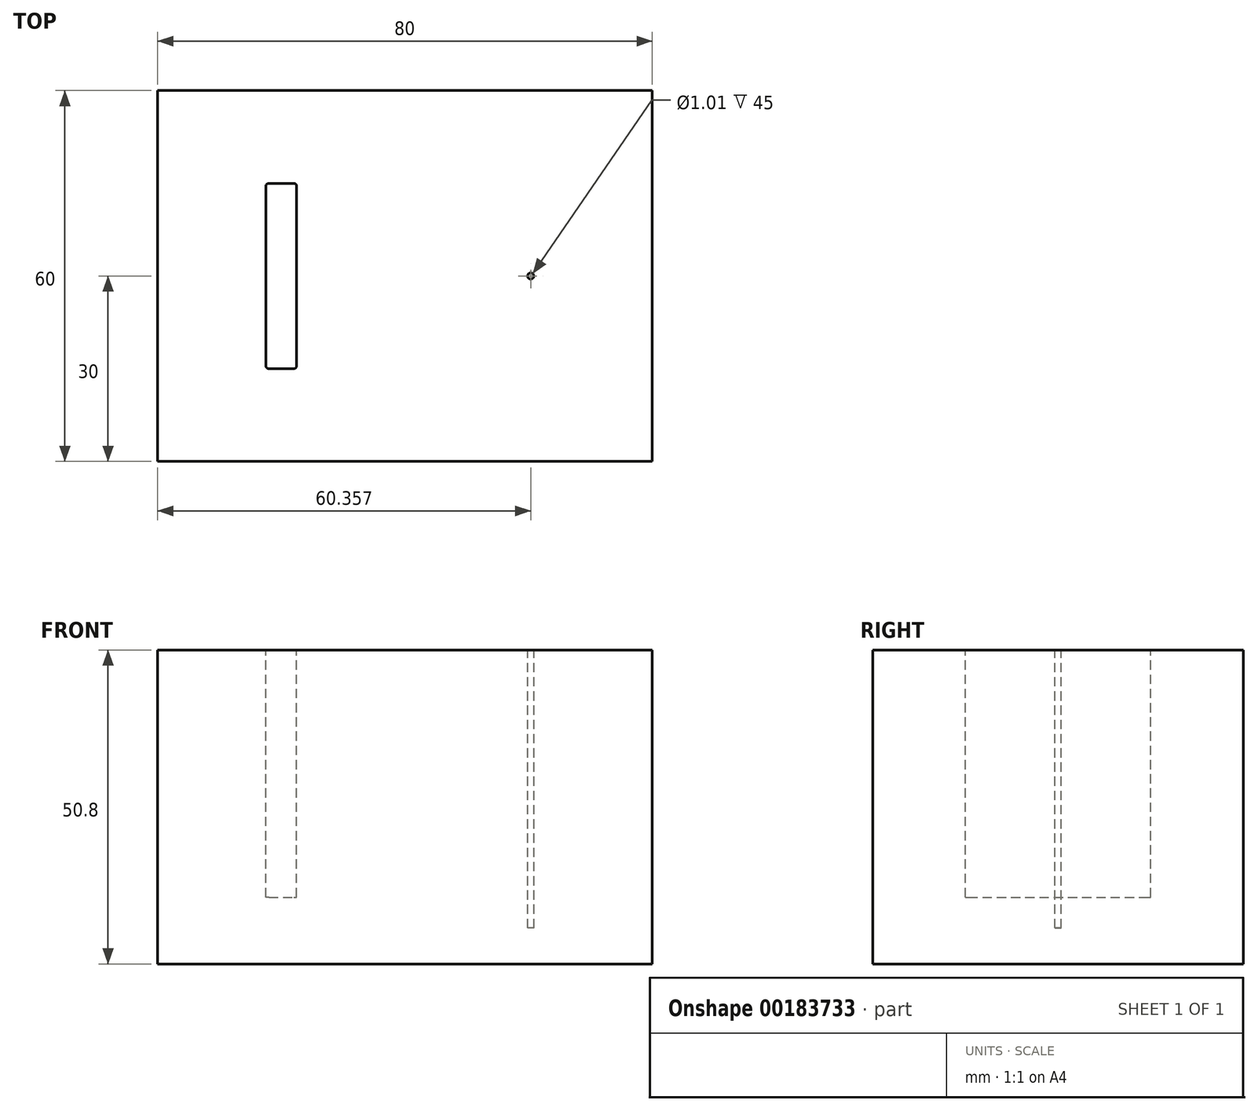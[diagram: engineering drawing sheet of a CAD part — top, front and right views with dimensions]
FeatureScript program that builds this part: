
annotation { "Feature Type Name" : "Feature", "Feature Type Description" : "" }
export const myFeature = defineFeature(function(context is Context, id is Id, definition is map)
    precondition{}
    {
        {
            var Q0;
            Q0=qCreatedBy(makeId("Top.planeOp"),FACE);
            var sketch = newSketch(context, id + "F0", { "sketchPlane" : qUnion([Q0])});
            skLineSegment(sketch, "E0.bottom", {"start": v(-40, -30) * mm, "end": v(40, -30) * mm});
            skLineSegment(sketch, "E0.top", {"start": v(-40, 30) * mm, "end": v(40, 30) * mm});
            skLineSegment(sketch, "E0.left", {"start": v(-40, -30) * mm, "end": v(-40, 30) * mm});
            skLineSegment(sketch, "E0.right", {"start": v(40, -30) * mm, "end": v(40, 30) * mm});
            skPoint(sketch, "E0.middle", {"position": v(0, 0) * mm});
            skSolve(sketch);
        }
        {
            var Q0;
            Q0=makeQuery(id+"F0.imprint","IMPRINT",FACE,{"disambiguationData":[TD([[makeQuery(id+"F0.imprint","IMPRINT",EDGE,{"derivedFrom":sQuery(id+"F0.wireOp",EDGE,"E0.bottom")}),1.0]])]});
            extrude(context, id + "F1", {"entities" : qUnion([Q0]), "depth" : 50.8 * mm});
        }
        {
            var Q0;
            Q0=makeQuery(id+"F1.opExtrude","CAP_FACE",FACE,{"disambiguationData":[OSD([sQuery(id+"F0.wireOp",EDGE,"E0.bottom"),sQuery(id+"F0.wireOp",EDGE,"E0.top"),sQuery(id+"F0.wireOp",EDGE,"E0.left"),sQuery(id+"F0.wireOp",EDGE,"E0.right")])],"isStart":false});
            var sketch = newSketch(context, id + "F2", { "sketchPlane" : qUnion([Q0])});
            skLineSegment(sketch, "E1.bottom", {"start": v(-22.5, -15) * mm, "end": v(-17.5, -15) * mm});
            skLineSegment(sketch, "E1.top", {"start": v(-22.5, 15) * mm, "end": v(-17.5, 15) * mm});
            skLineSegment(sketch, "E1.left", {"start": v(-22.5, -15) * mm, "end": v(-22.5, 15) * mm});
            skLineSegment(sketch, "E1.right", {"start": v(-17.5, -15) * mm, "end": v(-17.5, 15) * mm});
            skPoint(sketch, "E1.middle", {"position": v(-20, 0) * mm});
            skSolve(sketch);
        }
        {
            var Q0;
            Q0=makeQuery(id+"F2.imprint","IMPRINT",FACE,{"disambiguationData":[TD([[makeQuery(id+"F2.imprint","IMPRINT",EDGE,{"derivedFrom":sQuery(id+"F2.wireOp",EDGE,"E1.bottom")}),1.0]])]});
            extrude(context, id + "F3", {"entities" : qUnion([Q0]), "operationType" : NewBodyOperationType.REMOVE, "oppositeDirection" : true, "depth" : 40 * mm});
        }
        {
            var Q0;
            Q0=makeQuery(id+"F3.boolean.opBoolean","COPY",EDGE,{"derivedFrom":makeQuery(id+"F3.opExtrude","SWEPT_EDGE",EDGE,{"disambiguationData":[OSD([sQuery(id+"F2.wireOp",EDGE,"E1.top"),sQuery(id+"F2.wireOp",EDGE,"E1.left")])]})});
            var Q1;
            Q1=makeQuery(id+"F3.boolean.opBoolean","COPY",EDGE,{"derivedFrom":makeQuery(id+"F3.opExtrude","SWEPT_EDGE",EDGE,{"disambiguationData":[OSD([sQuery(id+"F2.wireOp",EDGE,"E1.top"),sQuery(id+"F2.wireOp",EDGE,"E1.right")])]})});
            var Q2;
            Q2=makeQuery(id+"F3.boolean.opBoolean","COPY",EDGE,{"derivedFrom":makeQuery(id+"F3.opExtrude","SWEPT_EDGE",EDGE,{"disambiguationData":[OSD([sQuery(id+"F2.wireOp",EDGE,"E1.bottom"),sQuery(id+"F2.wireOp",EDGE,"E1.left")])]})});
            var Q3;
            Q3=makeQuery(id+"F3.boolean.opBoolean","COPY",EDGE,{"derivedFrom":makeQuery(id+"F3.opExtrude","SWEPT_EDGE",EDGE,{"disambiguationData":[OSD([sQuery(id+"F2.wireOp",EDGE,"E1.bottom"),sQuery(id+"F2.wireOp",EDGE,"E1.right")])]})});
            fillet(context, id + "F4", {"entities" : qUnion([Q0, Q1, Q2, Q3]), "radius" : .5 * mm, "tangentPropagation" : true, "allowEdgeOverflow" : false});
        }
        {
            var Q0;
            Q0=makeQuery(id+"F1.opExtrude","CAP_FACE",FACE,{"disambiguationData":[OSD([sQuery(id+"F0.wireOp",EDGE,"E0.bottom"),sQuery(id+"F0.wireOp",EDGE,"E0.top"),sQuery(id+"F0.wireOp",EDGE,"E0.left"),sQuery(id+"F0.wireOp",EDGE,"E0.right")])],"isStart":false});
            var sketch = newSketch(context, id + "F5", { "sketchPlane" : qUnion([Q0])});
            skCircle(sketch, "E2", {"center": v(20.36, 0) * mm, "radius": 0.5 * mm});
            skSolve(sketch);
        }
        {
            var Q0;
            Q0=makeQuery(id+"F5.imprint","IMPRINT",FACE,{"disambiguationData":[TD([[makeQuery(id+"F5.imprint","IMPRINT",EDGE,{"derivedFrom":sQuery(id+"F5.wireOp",EDGE,"E2")}),1.0]])]});
            var Q1;
            Q1=sQuery(id+"F5.wireOp",EDGE,"E2");
            extrude(context, id + "F6", {"entities" : qUnion([Q0]), "operationType" : NewBodyOperationType.REMOVE, "surfaceEntities" : qUnion([Q1]), "oppositeDirection" : true, "depth" : 45 * mm});
        }
    });
